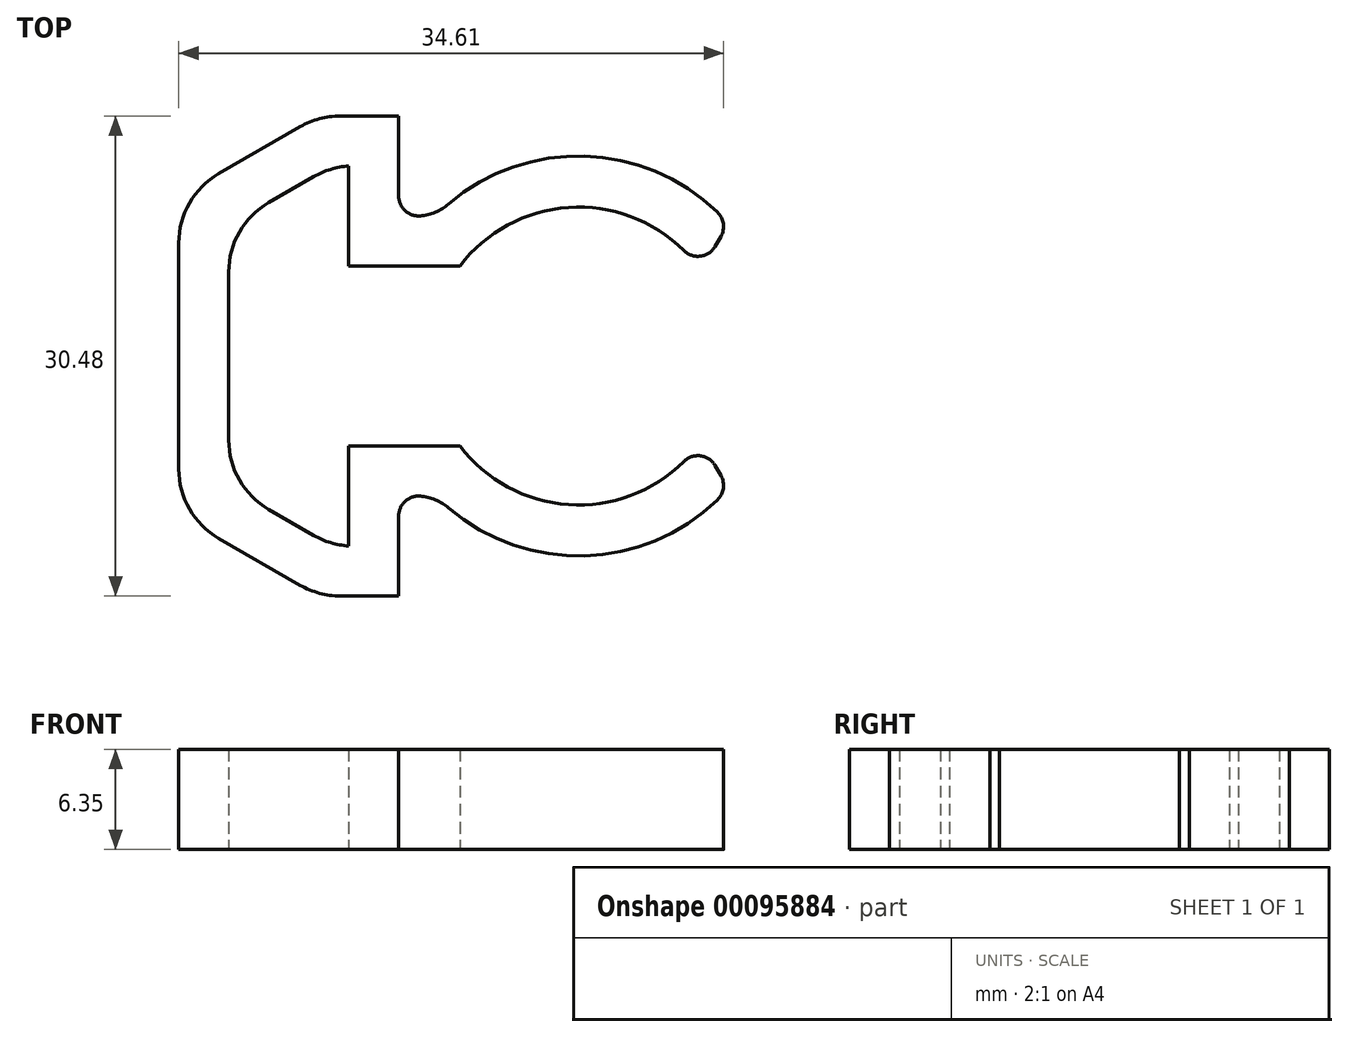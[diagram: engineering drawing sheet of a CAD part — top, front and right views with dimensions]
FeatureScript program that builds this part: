
annotation { "Feature Type Name" : "Feature", "Feature Type Description" : "" }
export const myFeature = defineFeature(function(context is Context, id is Id, definition is map)
    precondition{}
    {
        {
            var Q0;
            Q0=qCreatedBy(makeId("Top.planeOp"),FACE);
            var sketch = newSketch(context, id + "F0", { "sketchPlane" : qUnion([Q0])});
            skCircle(sketch, "E0", {"center": v(0, 0) * mm, "radius": 9.33 * mm, "construction": true});
            skArc(sketch, "E1", {"start": v(-7.54, -5.71) * mm, "mid": v(0.2, -9.46) * mm, "end": v(7.77, -5.4) * mm});
            skArc(sketch, "E2", {"start": v(-9.07, -8.9) * mm, "mid": v(0.33, -12.7) * mm, "end": v(9.51, -8.41) * mm});
            skLineSegment(sketch, "E3", {"start": v(-7.54, 5.72) * mm, "end": v(-14.6, 5.72) * mm});
            skLineSegment(sketch, "E4", {"start": v(-14.6, 5.72) * mm, "end": v(-14.6, 12.06) * mm});
            skLineSegment(sketch, "E5", {"start": v(-22.23, 8.27) * mm, "end": v(-22.23, -8.27) * mm});
            skLineSegment(sketch, "E6", {"start": v(-14.6, -12.06) * mm, "end": v(-14.6, -5.71) * mm});
            skLineSegment(sketch, "E7", {"start": v(-14.6, -5.71) * mm, "end": v(-7.54, -5.71) * mm});
            skLineSegment(sketch, "E8", {"start": v(-9.07, 8.9) * mm, "end": v(-11.43, 8.9) * mm});
            skLineSegment(sketch, "E9", {"start": v(-11.43, 8.9) * mm, "end": v(-11.43, 15.24) * mm});
            skLineSegment(sketch, "E10", {"start": v(-25.4, 10.1) * mm, "end": v(-25.4, -10.1) * mm});
            skLineSegment(sketch, "E11", {"start": v(-11.43, -15.24) * mm, "end": v(-11.43, -8.9) * mm});
            skLineSegment(sketch, "E12", {"start": v(-11.43, -8.9) * mm, "end": v(-9.07, -8.9) * mm});
            skLineSegment(sketch, "E13", {"start": v(-11.43, -15.24) * mm, "end": v(-16.51, -15.24) * mm});
            skLineSegment(sketch, "E14", {"start": v(-16.51, -15.24) * mm, "end": v(-25.4, -10.1) * mm});
            skLineSegment(sketch, "E15", {"start": v(-11.43, 15.24) * mm, "end": v(-16.51, 15.24) * mm});
            skLineSegment(sketch, "E16", {"start": v(-16.51, 15.24) * mm, "end": v(-25.4, 10.1) * mm});
            skLineSegment(sketch, "E17", {"start": v(-14.6, 12.06) * mm, "end": v(-15.66, 12.06) * mm});
            skLineSegment(sketch, "E18", {"start": v(-15.66, 12.06) * mm, "end": v(-22.23, 8.27) * mm});
            skLineSegment(sketch, "E19", {"start": v(-14.6, -12.06) * mm, "end": v(-15.66, -12.06) * mm});
            skLineSegment(sketch, "E20", {"start": v(-15.66, -12.07) * mm, "end": v(-22.23, -8.27) * mm});
            skPoint(sketch, "E21", {"position": v(-22.23, 0) * mm});
            skLineSegment(sketch, "E22", {"start": v(7.77, 5.4) * mm, "end": v(9.51, 8.41) * mm});
            skLineSegment(sketch, "E23.MirrorCS", {"start": v(7.77, -5.4) * mm, "end": v(9.51, -8.41) * mm});
            skArc(sketch, "E24.trimOffspring", {"start": v(7.77, 5.4) * mm, "mid": v(0.2, 9.46) * mm, "end": v(-7.54, 5.72) * mm});
            skArc(sketch, "E25.trimOffspring", {"start": v(9.51, 8.41) * mm, "mid": v(0.33, 12.7) * mm, "end": v(-9.07, 8.9) * mm});
            skSolve(sketch);
        }
        {
            var Q0;
            Q0=makeQuery(id+"F0.imprint","IMPRINT",FACE,{"disambiguationData":[TD([[makeQuery(id+"F0.imprint","IMPRINT",EDGE,{"derivedFrom":sQuery(id+"F0.wireOp",EDGE,"E1")}),-1.0]])]});
            extrude(context, id + "F1", {"entities" : qUnion([Q0]), "depth" : 6.35 * mm});
        }
        {
            var Q0;
            Q0=makeQuery(id+"F1.opExtrude","SWEPT_EDGE",EDGE,{"disambiguationData":[OSD([sQuery(id+"F0.wireOp",EDGE,"E19"),sQuery(id+"F0.wireOp",EDGE,"E20")])]});
            var Q1;
            Q1=makeQuery(id+"F1.opExtrude","SWEPT_EDGE",EDGE,{"disambiguationData":[OSD([sQuery(id+"F0.wireOp",EDGE,"E17"),sQuery(id+"F0.wireOp",EDGE,"E18")])]});
            var Q2;
            Q2=makeQuery(id+"F1.opExtrude","SWEPT_EDGE",EDGE,{"disambiguationData":[OSD([sQuery(id+"F0.wireOp",EDGE,"E5"),sQuery(id+"F0.wireOp",EDGE,"E18")])]});
            var Q3;
            Q3=makeQuery(id+"F1.opExtrude","SWEPT_EDGE",EDGE,{"disambiguationData":[OSD([sQuery(id+"F0.wireOp",EDGE,"E5"),sQuery(id+"F0.wireOp",EDGE,"E20")])]});
            var Q4;
            Q4=makeQuery(id+"F1.opExtrude","SWEPT_EDGE",EDGE,{"disambiguationData":[OSD([sQuery(id+"F0.wireOp",EDGE,"E10"),sQuery(id+"F0.wireOp",EDGE,"E14")])]});
            var Q5;
            Q5=makeQuery(id+"F1.opExtrude","SWEPT_EDGE",EDGE,{"disambiguationData":[OSD([sQuery(id+"F0.wireOp",EDGE,"E10"),sQuery(id+"F0.wireOp",EDGE,"E16")])]});
            var Q6;
            Q6=makeQuery(id+"F1.opExtrude","SWEPT_EDGE",EDGE,{"disambiguationData":[OSD([sQuery(id+"F0.wireOp",EDGE,"E13"),sQuery(id+"F0.wireOp",EDGE,"E14")])]});
            var Q7;
            Q7=makeQuery(id+"F1.opExtrude","SWEPT_EDGE",EDGE,{"disambiguationData":[OSD([sQuery(id+"F0.wireOp",EDGE,"E15"),sQuery(id+"F0.wireOp",EDGE,"E16")])]});
            fillet(context, id + "F2", {"entities" : qUnion([Q0, Q1, Q2, Q3, Q4, Q5, Q6, Q7]), "radius" : 5.08 * mm, "tangentPropagation" : true, "allowEdgeOverflow" : false});
        }
        {
            var Q0;
            Q0=makeQuery(id+"F1.opExtrude","SWEPT_EDGE",EDGE,{"disambiguationData":[OSD([sQuery(id+"F0.wireOp",EDGE,"E8"),sQuery(id+"F0.wireOp",EDGE,"E25.trimOffspring")])]});
            var Q1;
            Q1=makeQuery(id+"F1.opExtrude","SWEPT_EDGE",EDGE,{"disambiguationData":[OSD([sQuery(id+"F0.wireOp",EDGE,"E2"),sQuery(id+"F0.wireOp",EDGE,"E12")])]});
            fillet(context, id + "F3", {"entities" : qUnion([Q0, Q1]), "radius" : 3.17 * mm, "tangentPropagation" : true, "allowEdgeOverflow" : false});
        }
        {
            var Q0;
            Q0=makeQuery(id+"F1.opExtrude","SWEPT_EDGE",EDGE,{"disambiguationData":[OSD([sQuery(id+"F0.wireOp",EDGE,"E11"),sQuery(id+"F0.wireOp",EDGE,"E12")])]});
            var Q1;
            Q1=makeQuery(id+"F1.opExtrude","SWEPT_EDGE",EDGE,{"disambiguationData":[OSD([sQuery(id+"F0.wireOp",EDGE,"E8"),sQuery(id+"F0.wireOp",EDGE,"E9")])]});
            fillet(context, id + "F4", {"entities" : qUnion([Q0, Q1]), "radius" : 1.27 * mm, "allowEdgeOverflow" : false});
        }
        {
            var Q0;
            Q0=makeQuery(id+"F1.opExtrude","SWEPT_EDGE",EDGE,{"disambiguationData":[OSD([sQuery(id+"F0.wireOp",EDGE,"E1"),sQuery(id+"F0.wireOp",EDGE,"E23.MirrorCS")])]});
            var Q1;
            Q1=makeQuery(id+"F1.opExtrude","SWEPT_EDGE",EDGE,{"disambiguationData":[OSD([sQuery(id+"F0.wireOp",EDGE,"E2"),sQuery(id+"F0.wireOp",EDGE,"E23.MirrorCS")])]});
            var Q2;
            Q2=makeQuery(id+"F1.opExtrude","SWEPT_EDGE",EDGE,{"disambiguationData":[OSD([sQuery(id+"F0.wireOp",EDGE,"E22"),sQuery(id+"F0.wireOp",EDGE,"E25.trimOffspring")])]});
            var Q3;
            Q3=makeQuery(id+"F1.opExtrude","SWEPT_EDGE",EDGE,{"disambiguationData":[OSD([sQuery(id+"F0.wireOp",EDGE,"E22"),sQuery(id+"F0.wireOp",EDGE,"E24.trimOffspring")])]});
            fillet(context, id + "F5", {"entities" : qUnion([Q0, Q1, Q2, Q3]), "radius" : 1.27 * mm, "tangentPropagation" : true, "allowEdgeOverflow" : false});
        }
    });
